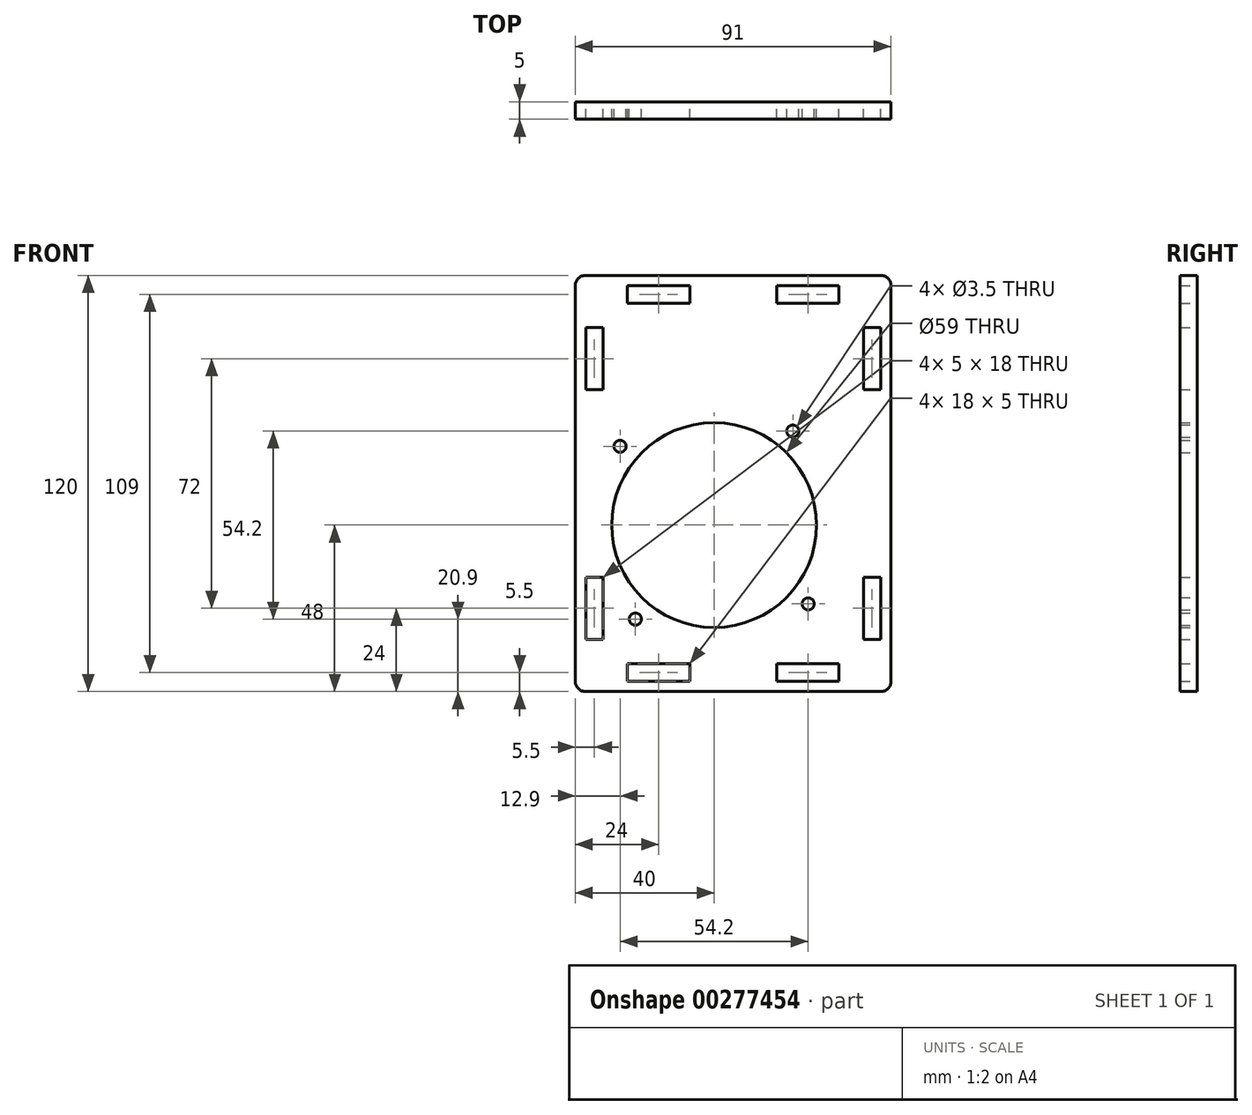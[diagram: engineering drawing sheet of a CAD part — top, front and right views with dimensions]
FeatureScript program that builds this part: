
annotation { "Feature Type Name" : "Feature", "Feature Type Description" : "" }
export const myFeature = defineFeature(function(context is Context, id is Id, definition is map)
    precondition{}
    {
        {
            var Q0;
            Q0=qCreatedBy(makeId("Front.planeOp"),FACE);
            var sketch = newSketch(context, id + "F0", { "sketchPlane" : qUnion([Q0])});
            skLineSegment(sketch, "E0.bottom", {"start": v(-42.5, 72) * mm, "end": v(42.5, 72) * mm});
            skLineSegment(sketch, "E0.top", {"start": v(-42.5, -48) * mm, "end": v(42.5, -48) * mm});
            skLineSegment(sketch, "E0.left", {"start": v(-45.5, 69) * mm, "end": v(-45.5, -45) * mm});
            skLineSegment(sketch, "E0.right", {"start": v(45.5, 69) * mm, "end": v(45.5, -45) * mm});
            skPoint(sketch, "E1.visualSharp", {"position": v(-45.5, 72) * mm});
            skArc(sketch, "E1.filletArc", {"start": v(-42.5, 72) * mm, "mid": v(-44.62, 71.12) * mm, "end": v(-45.5, 69) * mm});
            skPoint(sketch, "E2.visualSharp", {"position": v(45.5, 72) * mm});
            skArc(sketch, "E2.filletArc", {"start": v(45.5, 69) * mm, "mid": v(44.62, 71.12) * mm, "end": v(42.5, 72) * mm});
            skPoint(sketch, "E3.visualSharp", {"position": v(45.5, -48) * mm});
            skArc(sketch, "E3.filletArc", {"start": v(42.5, -48) * mm, "mid": v(44.62, -47.12) * mm, "end": v(45.5, -45) * mm});
            skPoint(sketch, "E4.visualSharp", {"position": v(-45.5, -48) * mm});
            skArc(sketch, "E4.filletArc", {"start": v(-45.5, -45) * mm, "mid": v(-44.62, -47.12) * mm, "end": v(-42.5, -48) * mm});
            skLineSegment(sketch, "E5.bottom", {"start": v(-30.5, 69) * mm, "end": v(-12.5, 69) * mm});
            skLineSegment(sketch, "E5.top", {"start": v(-30.5, 64) * mm, "end": v(-12.5, 64) * mm});
            skLineSegment(sketch, "E5.left", {"start": v(-30.5, 69) * mm, "end": v(-30.5, 64) * mm});
            skLineSegment(sketch, "E5.right", {"start": v(-12.5, 69) * mm, "end": v(-12.5, 64) * mm});
            skLineSegment(sketch, "E6.bottom", {"start": v(12.5, 69) * mm, "end": v(30.5, 69) * mm});
            skLineSegment(sketch, "E6.top", {"start": v(12.5, 64) * mm, "end": v(30.5, 64) * mm});
            skLineSegment(sketch, "E6.left", {"start": v(12.5, 69) * mm, "end": v(12.5, 64) * mm});
            skLineSegment(sketch, "E6.right", {"start": v(30.5, 69) * mm, "end": v(30.5, 64) * mm});
            skLineSegment(sketch, "E7.bottom", {"start": v(42.5, 57) * mm, "end": v(37.5, 57) * mm});
            skLineSegment(sketch, "E7.top", {"start": v(42.5, 39) * mm, "end": v(37.5, 39) * mm});
            skLineSegment(sketch, "E7.left", {"start": v(42.5, 57) * mm, "end": v(42.5, 39) * mm});
            skLineSegment(sketch, "E7.right", {"start": v(37.5, 57) * mm, "end": v(37.5, 39) * mm});
            skLineSegment(sketch, "E8.bottom", {"start": v(42.5, -15) * mm, "end": v(37.5, -15) * mm});
            skLineSegment(sketch, "E8.top", {"start": v(42.5, -33) * mm, "end": v(37.5, -33) * mm});
            skLineSegment(sketch, "E8.left", {"start": v(42.5, -15) * mm, "end": v(42.5, -33) * mm});
            skLineSegment(sketch, "E8.right", {"start": v(37.5, -15) * mm, "end": v(37.5, -33) * mm});
            skLineSegment(sketch, "E9.bottom", {"start": v(30.5, -45) * mm, "end": v(12.5, -45) * mm});
            skLineSegment(sketch, "E9.top", {"start": v(30.5, -40) * mm, "end": v(12.5, -40) * mm});
            skLineSegment(sketch, "E9.left", {"start": v(30.5, -45) * mm, "end": v(30.5, -40) * mm});
            skLineSegment(sketch, "E9.right", {"start": v(12.5, -45) * mm, "end": v(12.5, -40) * mm});
            skLineSegment(sketch, "E10.bottom", {"start": v(-12.5, -45) * mm, "end": v(-30.5, -45) * mm});
            skLineSegment(sketch, "E10.top", {"start": v(-12.5, -40) * mm, "end": v(-30.5, -40) * mm});
            skLineSegment(sketch, "E10.left", {"start": v(-12.5, -45) * mm, "end": v(-12.5, -40) * mm});
            skLineSegment(sketch, "E10.right", {"start": v(-30.5, -45) * mm, "end": v(-30.5, -40) * mm});
            skLineSegment(sketch, "E11.bottom", {"start": v(-37.5, -15) * mm, "end": v(-42.5, -15) * mm});
            skLineSegment(sketch, "E11.top", {"start": v(-37.5, -33) * mm, "end": v(-42.5, -33) * mm});
            skLineSegment(sketch, "E11.left", {"start": v(-37.5, -33) * mm, "end": v(-37.5, -15) * mm});
            skLineSegment(sketch, "E11.right", {"start": v(-42.5, -33) * mm, "end": v(-42.5, -15) * mm});
            skLineSegment(sketch, "E12.bottom", {"start": v(-37.5, 39) * mm, "end": v(-42.5, 39) * mm});
            skLineSegment(sketch, "E12.top", {"start": v(-37.5, 57) * mm, "end": v(-42.5, 57) * mm});
            skLineSegment(sketch, "E12.left", {"start": v(-37.5, 39) * mm, "end": v(-37.5, 57) * mm});
            skLineSegment(sketch, "E12.right", {"start": v(-42.5, 39) * mm, "end": v(-42.5, 57) * mm});
            skCircle(sketch, "E13", {"center": v(-5.5, 0) * mm, "radius": 29.5 * mm});
            skCircle(sketch, "E14", {"center": v(17.2, 27.1) * mm, "radius": 1.75 * mm});
            skCircle(sketch, "E15", {"center": v(-32.6, 22.7) * mm, "radius": 1.75 * mm});
            skCircle(sketch, "E16", {"center": v(-28.2, -27.1) * mm, "radius": 1.75 * mm});
            skCircle(sketch, "E17", {"center": v(21.6, -22.7) * mm, "radius": 1.75 * mm});
            skLineSegment(sketch, "E18", {"start": v(-45.5, 12) * mm, "end": v(45.5, 12) * mm, "construction": true});
            skSolve(sketch);
        }
        {
            var Q0;
            Q0=makeQuery(id+"F0.imprint","IMPRINT",FACE,{"disambiguationData":[TD([[makeQuery(id+"F0.imprint","IMPRINT",EDGE,{"derivedFrom":sQuery(id+"F0.wireOp",EDGE,"E0.bottom")}),-1.0]])]});
            extrude(context, id + "F1", {"entities" : qUnion([Q0]), "depth" : 5 * mm});
        }
    });
